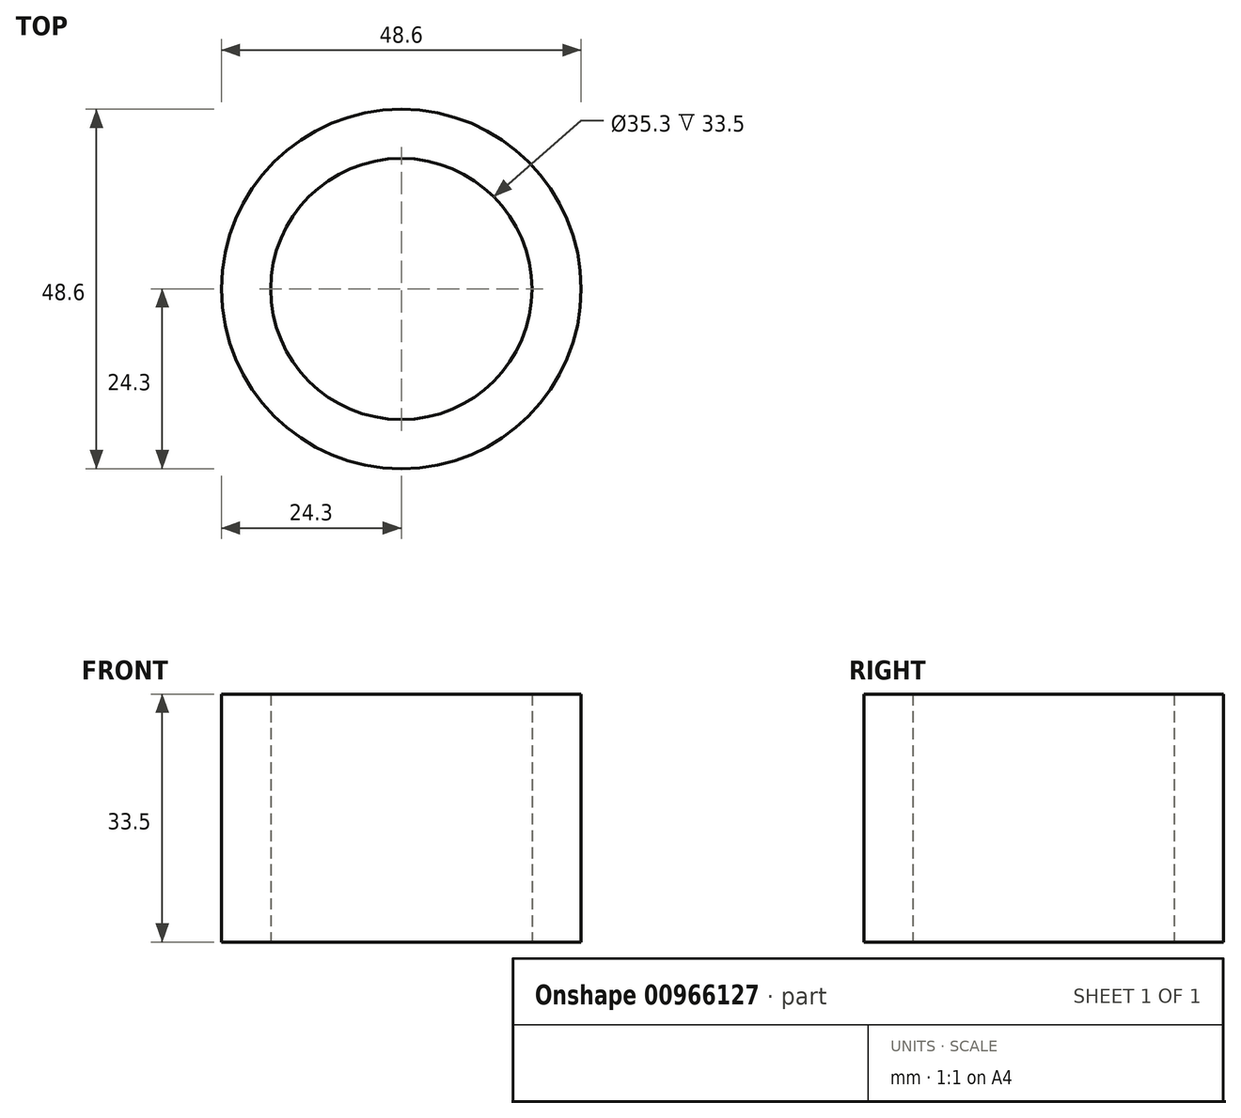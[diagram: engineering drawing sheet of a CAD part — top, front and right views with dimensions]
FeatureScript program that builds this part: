
annotation { "Feature Type Name" : "Feature", "Feature Type Description" : "" }
export const myFeature = defineFeature(function(context is Context, id is Id, definition is map)
    precondition{}
    {
        {
            var Q0;
            Q0=qCreatedBy(makeId("Top.planeOp"),FACE);
            var sketch = newSketch(context, id + "F0", { "sketchPlane" : qUnion([Q0])});
            skCircle(sketch, "E0", {"center": v(0, 0) * mm, "radius": 17.65 * mm});
            skCircle(sketch, "E1", {"center": v(0, 0) * mm, "radius": 24.3 * mm});
            skSolve(sketch);
        }
        {
            var Q0;
            Q0=makeQuery(id+"F0.imprint","IMPRINT",FACE,{"disambiguationData":[TD([[makeQuery(id+"F0.imprint","IMPRINT",EDGE,{"derivedFrom":sQuery(id+"F0.wireOp",EDGE,"E0")}),-1.0]])]});
            extrude(context, id + "F1", {"entities" : qUnion([Q0]), "depth" : 33.5 * mm, "offsetDistance" : 25 * mm});
        }
    });
